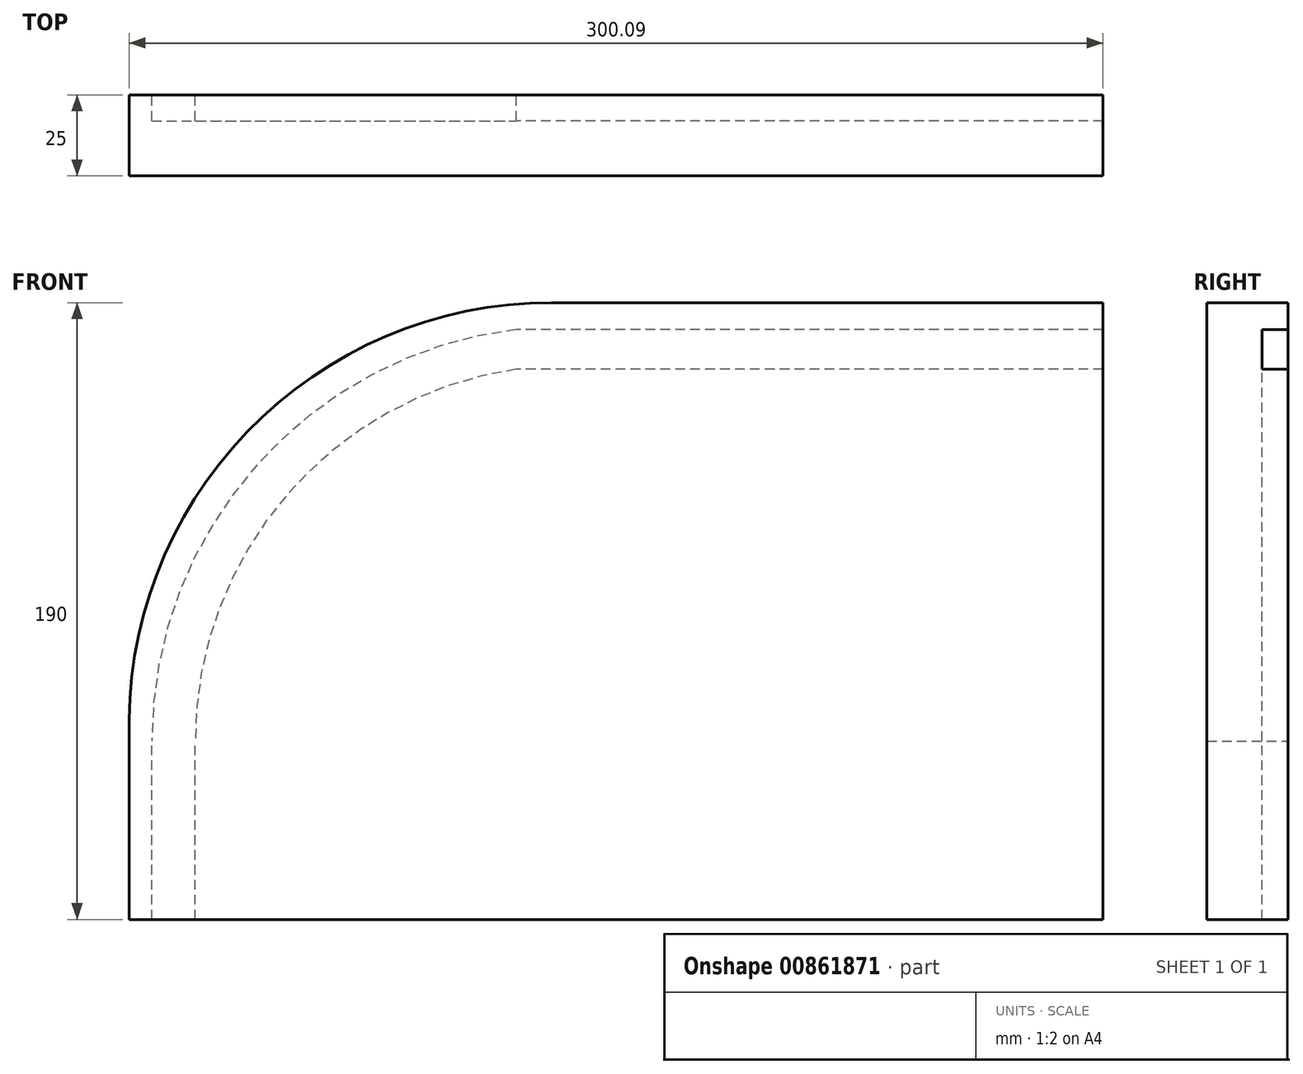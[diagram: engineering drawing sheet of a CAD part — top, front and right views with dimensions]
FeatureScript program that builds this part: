
annotation { "Feature Type Name" : "Feature", "Feature Type Description" : "" }
export const myFeature = defineFeature(function(context is Context, id is Id, definition is map)
    precondition{}
    {
        {
            var Q0;
            Q0=qCreatedBy(makeId("Front.planeOp"),FACE);
            var sketch = newSketch(context, id + "F0", { "sketchPlane" : qUnion([Q0])});
            skLineSegment(sketch, "E0", {"start": v(-119.18, 0) * mm, "end": v(180.82, 0) * mm});
            skLineSegment(sketch, "E1", {"start": v(-119.18, 0) * mm, "end": v(-119.18, 55) * mm});
            skLineSegment(sketch, "E2", {"start": v(180.82, 0) * mm, "end": v(180.82, 190) * mm});
            skLineSegment(sketch, "E3", {"start": v(10.82, 190) * mm, "end": v(180.82, 190) * mm});
            skArc(sketch, "E4", {"start": v(10.82, 190) * mm, "mid": v(-82.88, 150.15) * mm, "end": v(-119.18, 55) * mm});
            skSolve(sketch);
        }
        {
            var Q0;
            Q0 = qSketchRegion(id + "F0", true);
            extrude(context, id + "F1", {"entities" : qUnion([Q0]), "depth" : 25 * mm, "offsetDistance" : 25 * mm});
        }
        {
            var Q0;
            Q0=makeQuery(id+"F1.opExtrude","CAP_FACE",FACE,{"disambiguationData":[OSD([sQuery(id+"F0.wireOp",EDGE,"E0"),sQuery(id+"F0.wireOp",EDGE,"E1"),sQuery(id+"F0.wireOp",EDGE,"E2"),sQuery(id+"F0.wireOp",EDGE,"E3"),sQuery(id+"F0.wireOp",EDGE,"E4")])],"isStart":true});
            var sketch = newSketch(context, id + "F2", { "sketchPlane" : qUnion([Q0])});
            skPoint(sketch, "E5", {"position": v(-180.82, 181.74) * mm});
            skPoint(sketch, "E6", {"position": v(-180.82, 169.48) * mm});
            skLineSegment(sketch, "E7", {"start": v(-180.82, 181.74) * mm, "end": v(0, 181.74) * mm});
            skLineSegment(sketch, "E8", {"start": v(-180.82, 169.48) * mm, "end": v(0, 169.48) * mm});
            skPoint(sketch, "E9", {"position": v(112.2, 0) * mm});
            skPoint(sketch, "E10", {"position": v(98.85, 0) * mm});
            skLineSegment(sketch, "E11", {"start": v(112.2, 0) * mm, "end": v(112.2, 55) * mm});
            skLineSegment(sketch, "E12", {"start": v(98.85, 0) * mm, "end": v(98.85, 55) * mm});
            skArc(sketch, "E13", {"start": v(98.85, 55) * mm, "mid": v(70.72, 130.63) * mm, "end": v(0, 169.48) * mm});
            skArc(sketch, "E14", {"start": v(112.2, 55) * mm, "mid": v(80.12, 139.64) * mm, "end": v(0, 181.74) * mm});
            skSolve(sketch);
        }
        {
            var Q0;
            {var subQ1=sQuery(id+"F2.wireOp",EDGE,"E7");Q0=makeQuery(id+"F2.imprint","IMPRINT",FACE,{"disambiguationData":[TD([[makeQuery(id+"F2.imprint","IMPRINT",EDGE,{"derivedFrom":subQ1}),-1.0]])]});}
            extrude(context, id + "F3", {"entities" : qUnion([Q0]), "operationType" : NewBodyOperationType.REMOVE, "oppositeDirection" : true, "depth" : 8 * mm, "offsetDistance" : 25 * mm});
        }
    });
